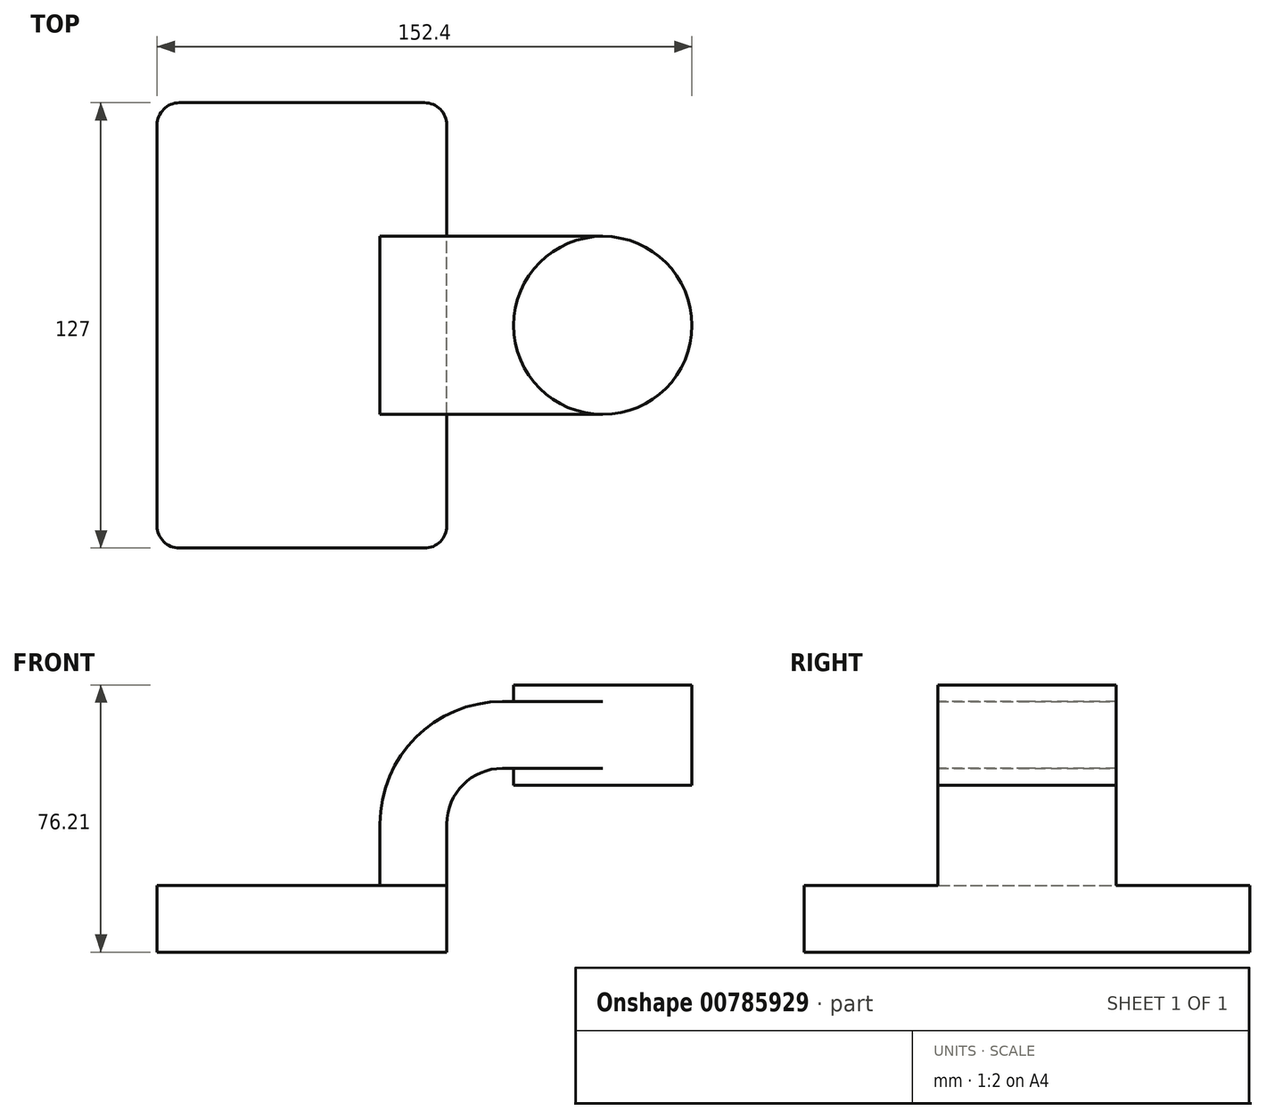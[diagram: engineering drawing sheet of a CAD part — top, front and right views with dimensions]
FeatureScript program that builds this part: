
annotation { "Feature Type Name" : "Feature", "Feature Type Description" : "" }
export const myFeature = defineFeature(function(context is Context, id is Id, definition is map)
    precondition{}
    {
        {
            var Q0;
            Q0=qCreatedBy(makeId("Front.planeOp"),FACE);
            var sketch = newSketch(context, id + "F0", { "sketchPlane" : qUnion([Q0])});
            skLineSegment(sketch, "E0.bottom", {"start": v(41.28, -9.52) * mm, "end": v(-41.28, -9.52) * mm});
            skLineSegment(sketch, "E0.top", {"start": v(41.28, 9.53) * mm, "end": v(-41.28, 9.53) * mm});
            skLineSegment(sketch, "E0.left", {"start": v(41.28, -9.52) * mm, "end": v(41.28, 9.53) * mm});
            skLineSegment(sketch, "E0.right", {"start": v(-41.28, -9.52) * mm, "end": v(-41.28, 9.53) * mm});
            skPoint(sketch, "E0.middle", {"position": v(0, 0) * mm});
            skLineSegment(sketch, "E1.bottom", {"start": v(111.12, 38.1) * mm, "end": v(60.32, 38.1) * mm});
            skLineSegment(sketch, "E1.top", {"start": v(111.12, 66.68) * mm, "end": v(60.32, 66.68) * mm});
            skLineSegment(sketch, "E1.left", {"start": v(111.12, 38.1) * mm, "end": v(111.12, 66.68) * mm});
            skLineSegment(sketch, "E1.right", {"start": v(60.32, 38.1) * mm, "end": v(60.32, 66.68) * mm});
            skPoint(sketch, "E1.middle", {"position": v(85.72, 52.39) * mm});
            skLineSegment(sketch, "E2", {"start": v(41.28, 9.53) * mm, "end": v(41.28, 27) * mm});
            skArc(sketch, "E3", {"start": v(41.28, 27) * mm, "mid": v(45.92, 38.23) * mm, "end": v(57.15, 42.88) * mm});
            skLineSegment(sketch, "E4", {"start": v(57.15, 42.88) * mm, "end": v(85.72, 42.88) * mm});
            skLineSegment(sketch, "E5.0", {"start": v(57.15, 61.93) * mm, "end": v(85.72, 61.93) * mm});
            skArc(sketch, "E5.1", {"start": v(22.23, 27) * mm, "mid": v(32.45, 51.7) * mm, "end": v(57.15, 61.93) * mm});
            skLineSegment(sketch, "E5.2", {"start": v(22.22, 9.53) * mm, "end": v(22.22, 27) * mm});
            skLineSegment(sketch, "E6", {"start": v(85.72, 38.1) * mm, "end": v(85.72, 66.68) * mm});
            skFitSpline(sketch, "E7", {"points": [v(-41.28, 9.53) * mm, v(57.15, 61.93) * mm], "startDerivative": vector(1.52, 96.41) * mm, "endDerivative": vector(131.02, 0.08) * mm});
            skSolve(sketch);
        }
        {
            var Q0;
            Q0=makeQuery(id+"F0.imprint","IMPRINT",FACE,{"disambiguationData":[TD([[makeQuery(id+"F0.imprint","IMPRINT",EDGE,{"derivedFrom":sQuery(id+"F0.wireOp",EDGE,"E0.bottom")}),-1.0]])]});
            extrude(context, id + "F1", {"entities" : qUnion([Q0]), "endBound" : BoundingType.SYMMETRIC, "depth" : 127 * mm, "offsetDistance" : 25.4 * mm});
        }
        {
            var Q0;
            {var subQ1=sQuery(id+"F0.wireOp",EDGE,"E2");Q0=makeQuery(id+"F0.imprint","IMPRINT",FACE,{"disambiguationData":[TD([[makeQuery(id+"F0.imprint","IMPRINT",EDGE,{"derivedFrom":subQ1}),1.0]])]});}
            extrude(context, id + "F2", {"entities" : qUnion([Q0]), "operationType" : NewBodyOperationType.ADD, "endBound" : BoundingType.SYMMETRIC, "depth" : 50.8 * mm, "offsetDistance" : 25.4 * mm});
        }
        {
            var Q0;
            {var subQ0=sQuery(id+"F0.wireOp",EDGE,"E4");var subQ1=sQuery(id+"F0.wireOp",EDGE,"E1.right");var subQ2=makeQuery(id+"F0.imprint","INTERSECT",VERTEX,{"derivedFrom":[subQ1,subQ0]});Q0=makeQuery(id+"F0.imprint","IMPRINT",FACE,{"disambiguationData":[TD([[makeQuery(id+"F0.imprint","IMPRINT",EDGE,{"disambiguationData":[TD([[subQ2,-1.0]])],"derivedFrom":subQ1}),-1.0]])]});}
            extrude(context, id + "F3", {"entities" : qUnion([Q0]), "operationType" : NewBodyOperationType.ADD, "endBound" : BoundingType.SYMMETRIC, "depth" : 50.8 * mm, "offsetDistance" : 25.4 * mm});
        }
        {
            var Q0;
            Q0=makeQuery(id+"F0.imprint","IMPRINT",FACE,{"disambiguationData":[TD([[makeQuery(id+"F0.imprint","IMPRINT",EDGE,{"derivedFrom":sQuery(id+"F0.wireOp",EDGE,"E5.1")}),1.0]])]});
            extrude(context, id + "F4", {"entities" : qUnion([Q0]), "operationType" : NewBodyOperationType.ADD, "endBound" : BoundingType.SYMMETRIC, "depth" : 15.88 * mm, "offsetDistance" : 25.4 * mm});
        }
        {
            var Q0;
            {var subQ4=sQuery(id+"F0.wireOp",EDGE,"E1.left");Q0=makeQuery(id+"F0.imprint","IMPRINT",FACE,{"disambiguationData":[TD([[makeQuery(id+"F0.imprint","IMPRINT",EDGE,{"derivedFrom":subQ4}),1.0]])]});}
            var Q1;
            Q1=sQuery(id+"F0.wireOp",EDGE,"E6");
            revolve(context, id + "F5", {"operationType" : NewBodyOperationType.ADD, "surfaceOperationType" : NewSurfaceOperationType.NEW, "entities" : qUnion([Q0]), "axis" : qUnion([Q1]), "revolveType" : RevolveType.FULL});
        }
        {
            var Q0;
            Q0=makeQuery(id+"F1.opExtrude","CAP_EDGE",EDGE,{"disambiguationData":[OSD([sQuery(id+"F0.wireOp",EDGE,"E0.right")])],"isStart":false});
            var Q1;
            Q1=makeQuery(id+"F1.opExtrude","CAP_EDGE",EDGE,{"disambiguationData":[OSD([sQuery(id+"F0.wireOp",EDGE,"E0.left")])],"isStart":false});
            var Q2;
            Q2=makeQuery(id+"F1.opExtrude","CAP_EDGE",EDGE,{"disambiguationData":[OSD([sQuery(id+"F0.wireOp",EDGE,"E0.left")])],"isStart":true});
            var Q3;
            Q3=makeQuery(id+"F1.opExtrude","CAP_EDGE",EDGE,{"disambiguationData":[OSD([sQuery(id+"F0.wireOp",EDGE,"E0.right")])],"isStart":true});
            fillet(context, id + "F6", {"entities" : qUnion([Q0, Q1, Q2, Q3]), "radius" : 6.35 * mm, "tangentPropagation" : true, "allowEdgeOverflow" : false});
        }
    });
